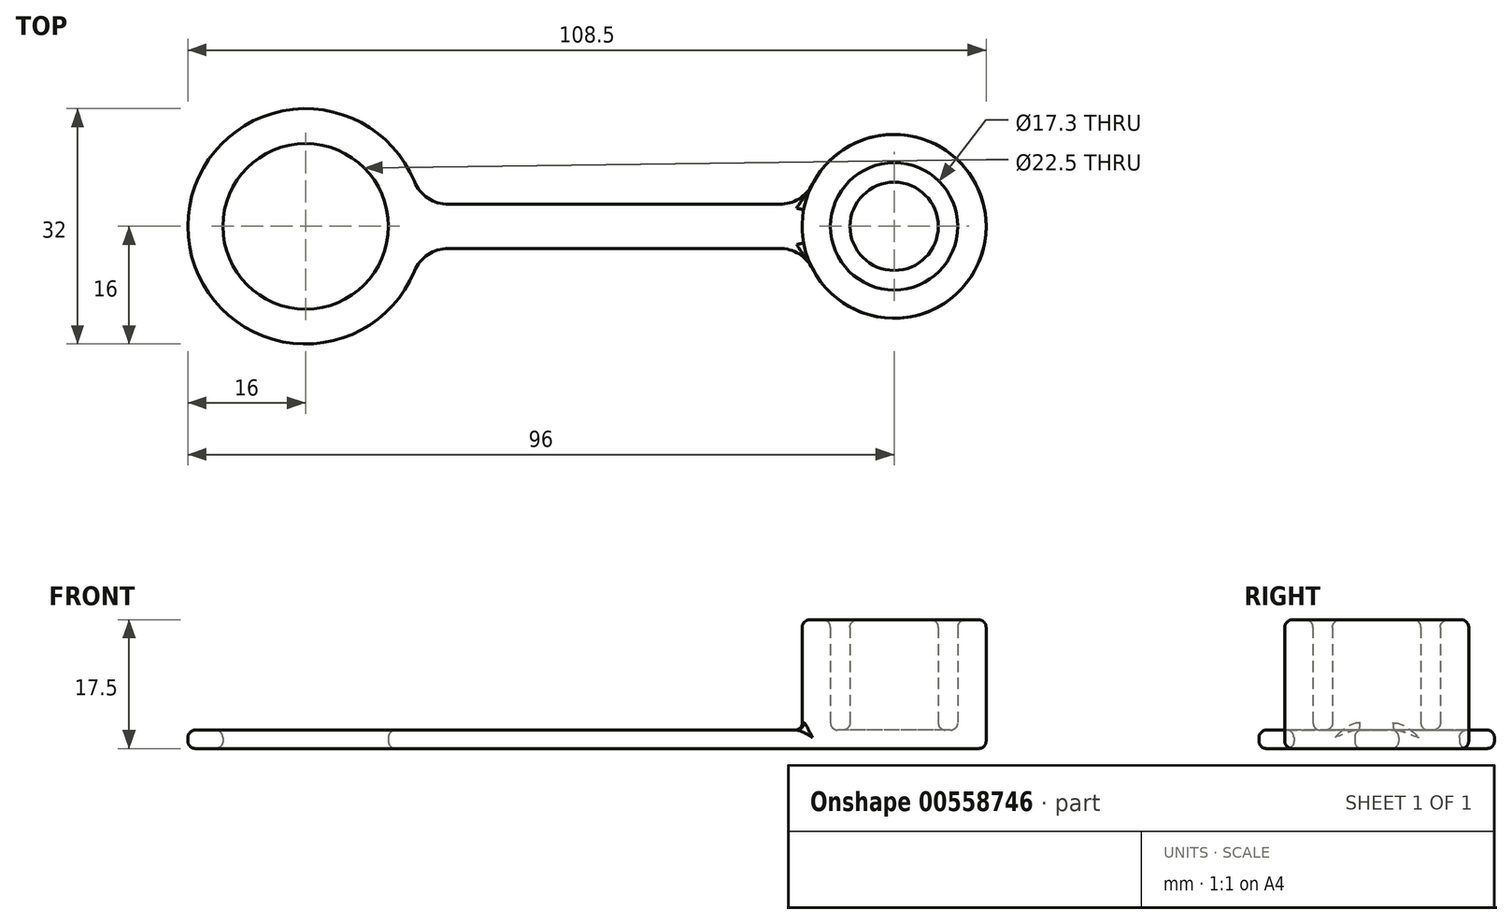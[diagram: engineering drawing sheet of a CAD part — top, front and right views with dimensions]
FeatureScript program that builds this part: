
annotation { "Feature Type Name" : "Feature", "Feature Type Description" : "" }
export const myFeature = defineFeature(function(context is Context, id is Id, definition is map)
    precondition{}
    {
        {
            var Q0;
            Q0=qCreatedBy(makeId("Top.planeOp"),FACE);
            var sketch = newSketch(context, id + "F0", { "sketchPlane" : qUnion([Q0])});
            skCircle(sketch, "E0", {"center": v(-80, 0) * mm, "radius": 11.25 * mm});
            skArc(sketch, "E1", {"start": v(-65.2, 6.1) * mm, "mid": v(-96, 0) * mm, "end": v(-65.2, -6.1) * mm});
            skArc(sketch, "E2.0", {"start": v(-11.12, -5.71) * mm, "mid": v(12.5, 0) * mm, "end": v(-11.12, 5.71) * mm});
            skLineSegment(sketch, "E3", {"start": v(-60.58, -3) * mm, "end": v(-15.56, -3) * mm});
            skLineSegment(sketch, "E4.MirrorCS", {"start": v(-60.58, 3) * mm, "end": v(-15.56, 3) * mm});
            skPoint(sketch, "E5.visualSharp", {"position": v(-64.28, -3) * mm});
            skArc(sketch, "E5.filletArc", {"start": v(-60.58, -3) * mm, "mid": v(-63.37, -3.85) * mm, "end": v(-65.2, -6.1) * mm});
            skPoint(sketch, "E6.visualSharp", {"position": v(-12.13, -3) * mm});
            skArc(sketch, "E6.filletArc", {"start": v(-11.12, -5.71) * mm, "mid": v(-12.96, -3.73) * mm, "end": v(-15.56, -3) * mm});
            skPoint(sketch, "E7.visualSharp", {"position": v(-12.13, 3) * mm});
            skArc(sketch, "E7.filletArc", {"start": v(-15.56, 3) * mm, "mid": v(-12.96, 3.73) * mm, "end": v(-11.12, 5.71) * mm});
            skPoint(sketch, "E8.visualSharp", {"position": v(-64.28, 3) * mm});
            skArc(sketch, "E8.filletArc", {"start": v(-65.2, 6.1) * mm, "mid": v(-63.37, 3.85) * mm, "end": v(-60.58, 3) * mm});
            skSolve(sketch);
        }
        {
            var Q0;
            Q0 = qSketchRegion(id + "F0", true);
            extrude(context, id + "F1", {"entities" : qUnion([Q0]), "depth" : 2.5 * mm, "offsetDistance" : 25 * mm});
        }
        {
            var Q0;
            Q0=makeQuery(id+"F1.opExtrude","CAP_FACE",FACE,{"disambiguationData":[OSD([sQuery(id+"F0.wireOp",EDGE,"E0"),sQuery(id+"F0.wireOp",EDGE,"E1"),sQuery(id+"F0.wireOp",EDGE,"E2.0"),sQuery(id+"F0.wireOp",EDGE,"E3"),sQuery(id+"F0.wireOp",EDGE,"E4.MirrorCS"),sQuery(id+"F0.wireOp",EDGE,"E5.filletArc"),sQuery(id+"F0.wireOp",EDGE,"E6.filletArc"),sQuery(id+"F0.wireOp",EDGE,"E7.filletArc"),sQuery(id+"F0.wireOp",EDGE,"E8.filletArc")])],"isStart":false});
            var sketch = newSketch(context, id + "F2", { "sketchPlane" : qUnion([Q0])});
            skCircle(sketch, "E9", {"center": v(0, 0) * mm, "radius": 6 * mm});
            skSolve(sketch);
        }
        {
            var Q0;
            Q0 = qSketchRegion(id + "F2", true);
            extrude(context, id + "F3", {"entities" : qUnion([Q0]), "operationType" : NewBodyOperationType.ADD, "depth" : 15 * mm, "offsetDistance" : 25 * mm});
        }
        {
            var Q0;
            Q0=makeQuery(id+"F1.opExtrude","CAP_FACE",FACE,{"disambiguationData":[OSD([sQuery(id+"F0.wireOp",EDGE,"E0"),sQuery(id+"F0.wireOp",EDGE,"E1"),sQuery(id+"F0.wireOp",EDGE,"E2.0"),sQuery(id+"F0.wireOp",EDGE,"E3"),sQuery(id+"F0.wireOp",EDGE,"E4.MirrorCS"),sQuery(id+"F0.wireOp",EDGE,"E5.filletArc"),sQuery(id+"F0.wireOp",EDGE,"E6.filletArc"),sQuery(id+"F0.wireOp",EDGE,"E7.filletArc"),sQuery(id+"F0.wireOp",EDGE,"E8.filletArc")])],"isStart":false});
            var sketch = newSketch(context, id + "F4", { "sketchPlane" : qUnion([Q0])});
            skCircle(sketch, "E10", {"center": v(0, 0) * mm, "radius": 12.5 * mm});
            skCircle(sketch, "E11", {"center": v(0, 0) * mm, "radius": 8.65 * mm});
            skSolve(sketch);
        }
        {
            var Q0;
            Q0 = qSketchRegion(id + "F4", true);
            extrude(context, id + "F5", {"entities" : qUnion([Q0]), "operationType" : NewBodyOperationType.ADD, "depth" : 15 * mm, "offsetDistance" : 25 * mm});
        }
        {
            var Q0;
            {var subQ0=sQuery(id+"F0.wireOp",EDGE,"E2.0");var subQ1=sQuery(id+"F0.wireOp",EDGE,"E1");var subQ2=sQuery(id+"F0.wireOp",EDGE,"E3");var subQ3=sQuery(id+"F0.wireOp",EDGE,"E0");var subQ4=sQuery(id+"F0.wireOp",EDGE,"E4.MirrorCS");var subQ5=sQuery(id+"F0.wireOp",EDGE,"E5.filletArc");var subQ6=sQuery(id+"F0.wireOp",EDGE,"E6.filletArc");var subQ7=sQuery(id+"F0.wireOp",EDGE,"E7.filletArc");var subQ8=sQuery(id+"F0.wireOp",EDGE,"E8.filletArc");Q0=makeQuery(id+"F5.boolean.opBoolean","SPLIT",FACE,{"disambiguationData":[TD([makeQuery(id+"F1.opExtrude","SWEPT_FACE",FACE,{"disambiguationData":[OSD([subQ3])]})])],"derivedFrom":makeQuery(id+"F1.opExtrude","CAP_FACE",FACE,{"disambiguationData":[OSD([subQ3,subQ1,subQ0,subQ2,subQ4,subQ5,subQ6,subQ7,subQ8])],"isStart":false})});}
            var Q1;
            Q1=makeQuery(id+"F1.opExtrude","CAP_FACE",FACE,{"disambiguationData":[OSD([sQuery(id+"F0.wireOp",EDGE,"E0"),sQuery(id+"F0.wireOp",EDGE,"E1"),sQuery(id+"F0.wireOp",EDGE,"E2.0"),sQuery(id+"F0.wireOp",EDGE,"E3"),sQuery(id+"F0.wireOp",EDGE,"E4.MirrorCS"),sQuery(id+"F0.wireOp",EDGE,"E5.filletArc"),sQuery(id+"F0.wireOp",EDGE,"E6.filletArc"),sQuery(id+"F0.wireOp",EDGE,"E7.filletArc"),sQuery(id+"F0.wireOp",EDGE,"E8.filletArc")])],"isStart":true});
            var Q2;
            Q2=makeQuery(id+"F5.opExtrude","CAP_FACE",FACE,{"disambiguationData":[OSD([sQuery(id+"F4.wireOp",EDGE,"E10"),sQuery(id+"F4.wireOp",EDGE,"E11")])],"isStart":false});
            var Q3;
            Q3=makeQuery(id+"F3.opExtrude","CAP_FACE",FACE,{"disambiguationData":[OSD([sQuery(id+"F2.wireOp",EDGE,"E9")])],"isStart":false});
            var Q4;
            Q4=makeQuery(id+"F5.boolean.opBoolean","SPLIT",FACE,{"disambiguationData":[TD([makeQuery(id+"F3.opExtrude","SWEPT_FACE",FACE,{"disambiguationData":[OSD([sQuery(id+"F2.wireOp",EDGE,"E9")])]})])],"derivedFrom":makeQuery(id+"F1.opExtrude","CAP_FACE",FACE,{"disambiguationData":[OSD([sQuery(id+"F0.wireOp",EDGE,"E0"),sQuery(id+"F0.wireOp",EDGE,"E1"),sQuery(id+"F0.wireOp",EDGE,"E2.0"),sQuery(id+"F0.wireOp",EDGE,"E3"),sQuery(id+"F0.wireOp",EDGE,"E4.MirrorCS"),sQuery(id+"F0.wireOp",EDGE,"E5.filletArc"),sQuery(id+"F0.wireOp",EDGE,"E6.filletArc"),sQuery(id+"F0.wireOp",EDGE,"E7.filletArc"),sQuery(id+"F0.wireOp",EDGE,"E8.filletArc")])],"isStart":false})});
            fillet(context, id + "F6", {"entities" : qUnion([Q0, Q1, Q2, Q3, Q4]), "radius" : 1 * mm, "tangentPropagation" : true, "allowEdgeOverflow" : false});
        }
    });
